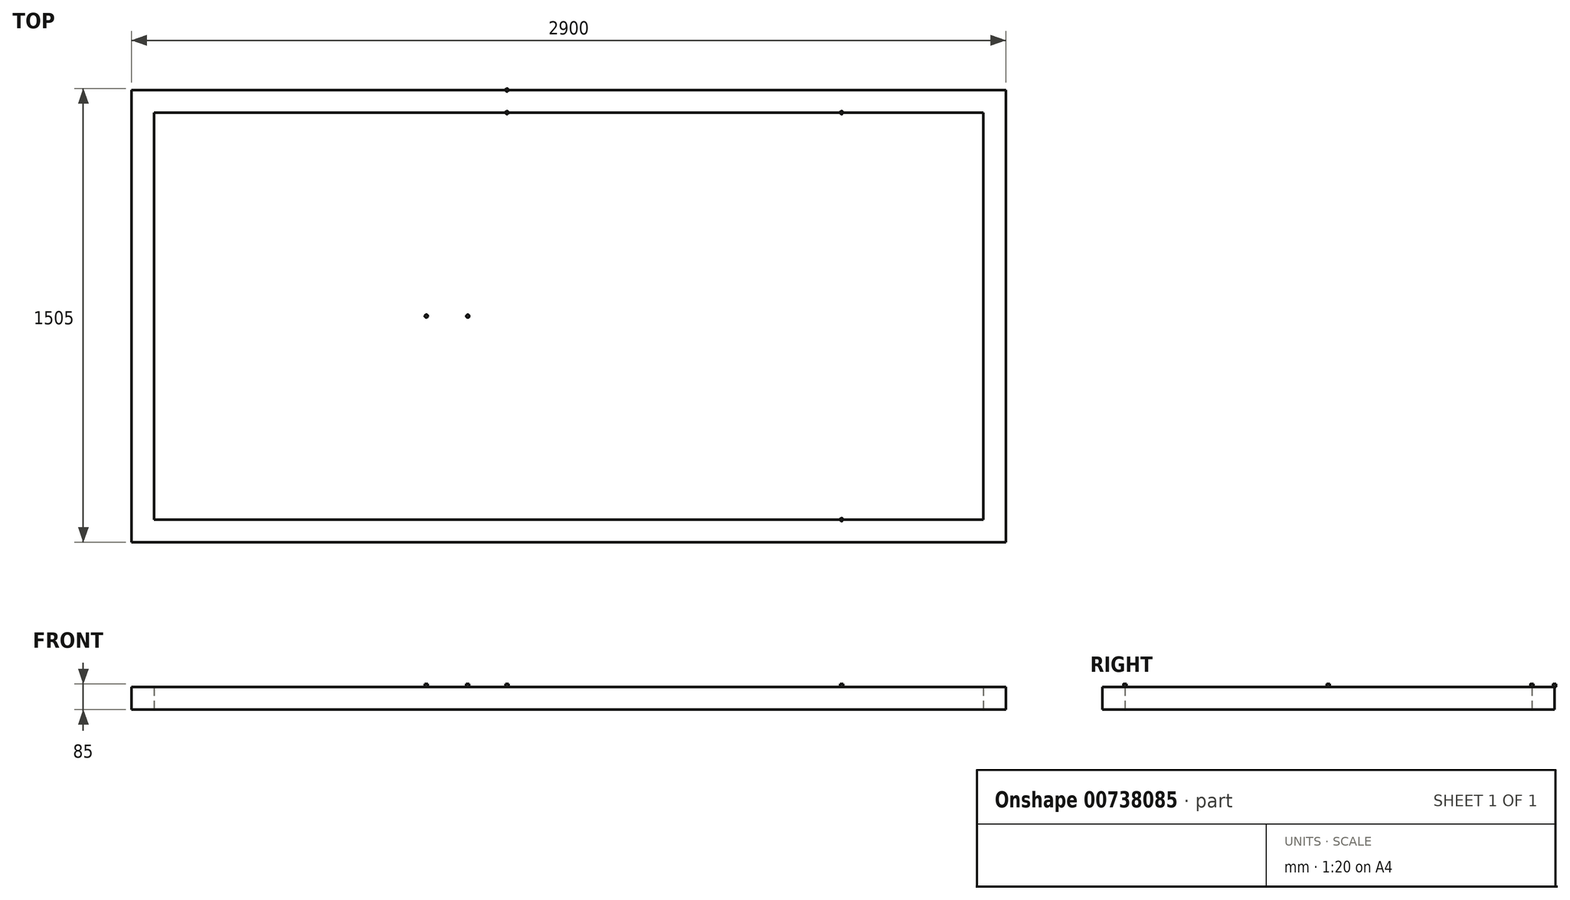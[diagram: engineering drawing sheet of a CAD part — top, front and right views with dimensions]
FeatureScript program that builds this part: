
annotation { "Feature Type Name" : "Feature", "Feature Type Description" : "" }
export const myFeature = defineFeature(function(context is Context, id is Id, definition is map)
    precondition{}
    {
        {
            var Q0;
            Q0=qCreatedBy(makeId("Top.planeOp"),FACE);
            var sketch = newSketch(context, id + "F0", { "sketchPlane" : qUnion([Q0])});
            skPoint(sketch, "E0.middle", {"position": v(0, 0) * mm});
            skLineSegment(sketch, "E1.bottom", {"start": v(-1450, -750) * mm, "end": v(1450, -750) * mm});
            skLineSegment(sketch, "E1.top", {"start": v(-1450, 750) * mm, "end": v(1450, 750) * mm});
            skLineSegment(sketch, "E1.left", {"start": v(-1450, -750) * mm, "end": v(-1450, 750) * mm});
            skLineSegment(sketch, "E1.right", {"start": v(1450, -750) * mm, "end": v(1450, 750) * mm});
            skPoint(sketch, "E2.endSnap0", {"position": v(-1450, 0) * mm});
            skLineSegment(sketch, "E3.0", {"start": v(-1375, -675) * mm, "end": v(-1375, 675) * mm});
            skLineSegment(sketch, "E3.1", {"start": v(-1375, -675) * mm, "end": v(1375, -675) * mm});
            skLineSegment(sketch, "E3.2", {"start": v(1375, -675) * mm, "end": v(1375, 675) * mm});
            skLineSegment(sketch, "E3.3", {"start": v(-1375, 675) * mm, "end": v(1375, 675) * mm});
            skLineSegment(sketch, "E4", {"start": v(-1375, -675) * mm, "end": v(-435, -675) * mm});
            skLineSegment(sketch, "E5.bottom", {"start": v(-435, -675) * mm, "end": v(-510, -675) * mm});
            skLineSegment(sketch, "E5.top", {"start": v(-435, 675) * mm, "end": v(-510, 675) * mm});
            skLineSegment(sketch, "E5.left", {"start": v(-435, -675) * mm, "end": v(-435, 675) * mm});
            skLineSegment(sketch, "E5.right", {"start": v(-510, -675) * mm, "end": v(-510, 675) * mm});
            skLineSegment(sketch, "E6", {"start": v(1375, -675) * mm, "end": v(435, -675) * mm});
            skLineSegment(sketch, "E7.bottom", {"start": v(435, -675) * mm, "end": v(510, -675) * mm});
            skLineSegment(sketch, "E7.top", {"start": v(435, 675) * mm, "end": v(510, 675) * mm});
            skLineSegment(sketch, "E7.left", {"start": v(435, -675) * mm, "end": v(435, 675) * mm});
            skLineSegment(sketch, "E7.right", {"start": v(510, -675) * mm, "end": v(510, 675) * mm});
            skSolve(sketch);
        }
        {
            var Q0;
            Q0=qSketchRegion(id+"F0",true);
            var Q1;
            Q1=makeQuery(id+"F0.imprint","IMPRINT",FACE,{"disambiguationData":[TD([[makeQuery(id+"F0.imprint","IMPRINT",EDGE,{"derivedFrom":sQuery(id+"F0.wireOp",EDGE,"E5.bottom")}),-1.0]])]});
            var Q2;
            Q2=makeQuery(id+"F0.imprint","IMPRINT",FACE,{"disambiguationData":[TD([[makeQuery(id+"F0.imprint","IMPRINT",EDGE,{"derivedFrom":sQuery(id+"F0.wireOp",EDGE,"E7.bottom")}),1.0]])]});
            extrude(context, id + "F1", {"entities" : qUnion([Q0, Q1, Q2]), "depth" : 75 * mm, "offsetDistance" : 25 * mm});
        }
        {
            var Q0;
            Q0=makeQuery(id+"F1.opExtrude","CAP_FACE",FACE,{"disambiguationData":[OSD([sQuery(id+"F0.wireOp",EDGE,"E1.bottom"),sQuery(id+"F0.wireOp",EDGE,"E1.top"),sQuery(id+"F0.wireOp",EDGE,"E1.left"),sQuery(id+"F0.wireOp",EDGE,"E1.right"),sQuery(id+"F0.wireOp",EDGE,"E3.0"),sQuery(id+"F0.wireOp",EDGE,"E3.1"),sQuery(id+"F0.wireOp",EDGE,"E3.2"),sQuery(id+"F0.wireOp",EDGE,"E3.3"),sQuery(id+"F0.wireOp",EDGE,"E4"),sQuery(id+"F0.wireOp",EDGE,"E5.left"),sQuery(id+"F0.wireOp",EDGE,"E5.right"),sQuery(id+"F0.wireOp",EDGE,"E6"),sQuery(id+"F0.wireOp",EDGE,"E7.left"),sQuery(id+"F0.wireOp",EDGE,"E7.right")])],"isStart":false});
            var sketch = newSketch(context, id + "F2", { "sketchPlane" : qUnion([Q0])});
            skLineSegment(sketch, "E8", {"start": v(-435, 0) * mm, "end": v(-472.5, 0) * mm});
            skCircle(sketch, "E9", {"center": v(-472.5, 0) * mm, "radius": 5 * mm});
            skLineSegment(sketch, "E10", {"start": v(-435, 0) * mm, "end": v(-335, 0) * mm});
            skCircle(sketch, "E11", {"center": v(-335, 0) * mm, "radius": 5 * mm});
            skLineSegment(sketch, "E12", {"start": v(-1375, 675) * mm, "end": v(905, 675) * mm});
            skCircle(sketch, "E13", {"center": v(905, 675) * mm, "radius": 5 * mm});
            skLineSegment(sketch, "E14", {"start": v(-1375, -675) * mm, "end": v(905, -675) * mm});
            skCircle(sketch, "E15", {"center": v(905, -675) * mm, "radius": 5 * mm});
            skLineSegment(sketch, "E16", {"start": v(905, 675) * mm, "end": v(-205, 675) * mm});
            skCircle(sketch, "E17", {"center": v(-205, 675) * mm, "radius": 5 * mm});
            skLineSegment(sketch, "E18", {"start": v(-205, 675) * mm, "end": v(-205, 750) * mm});
            skCircle(sketch, "E19", {"center": v(-205, 750) * mm, "radius": 5 * mm});
            skSolve(sketch);
        }
        {
            var Q0;
            Q0=qSketchRegion(id+"F2",true);
            extrude(context, id + "F3", {"entities" : qUnion([Q0]), "operationType" : NewBodyOperationType.ADD, "depth" : 10 * mm, "offsetDistance" : 25 * mm});
        }
        {
            var Q0;
            Q0=qSketchRegion(id+"F2",true);
            extrude(context, id + "F4", {"entities" : qUnion([Q0]), "depth" : 10 * mm, "offsetDistance" : 25 * mm});
        }
    });
